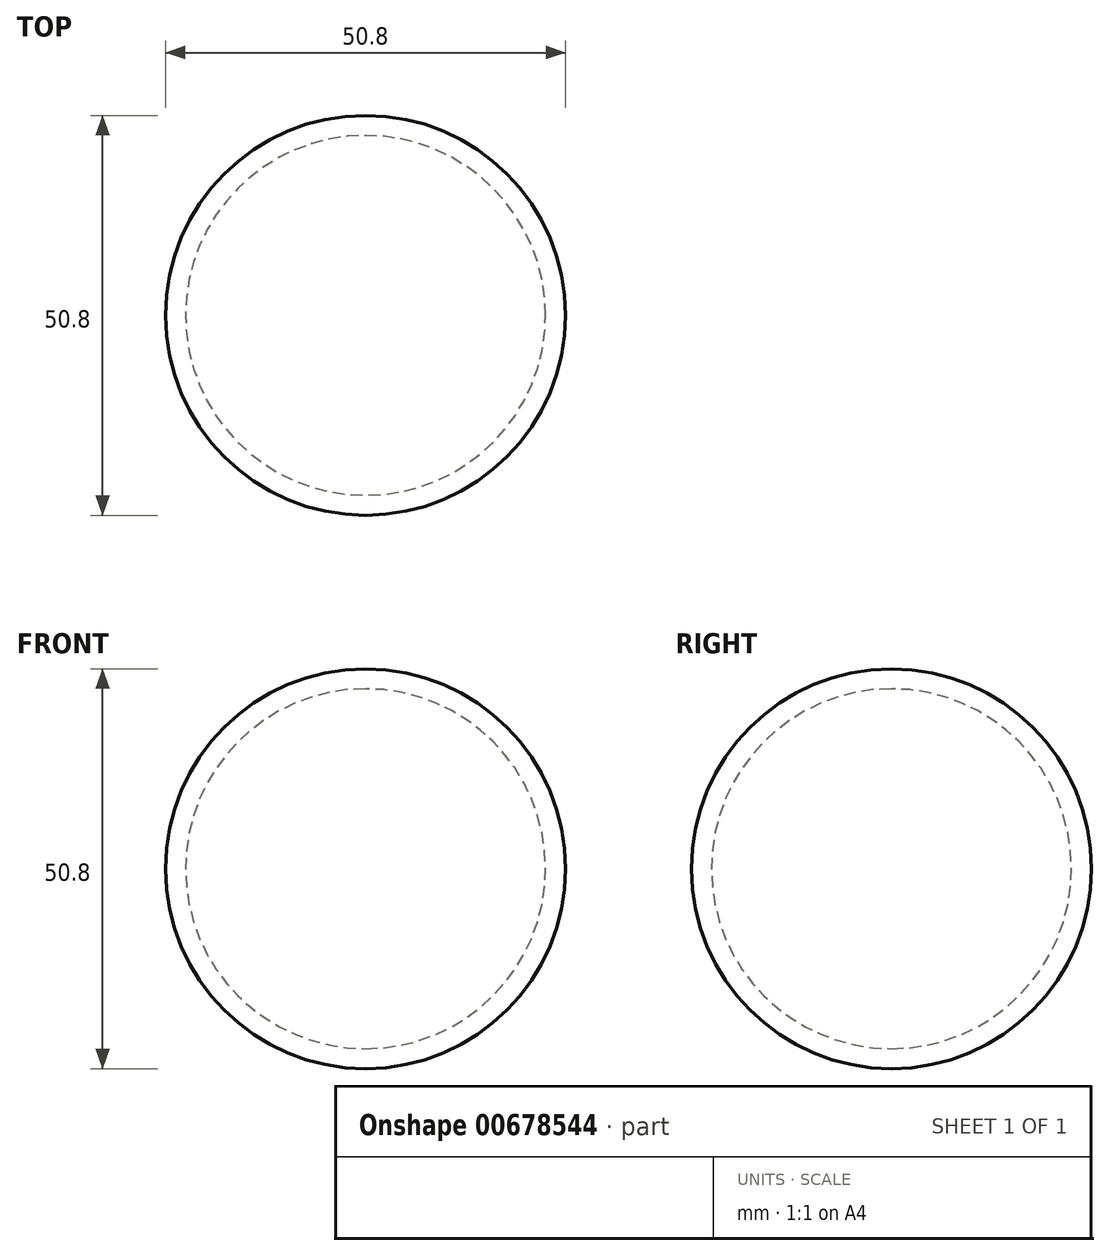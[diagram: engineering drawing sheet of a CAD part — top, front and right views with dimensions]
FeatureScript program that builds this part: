
annotation { "Feature Type Name" : "Feature", "Feature Type Description" : "" }
export const myFeature = defineFeature(function(context is Context, id is Id, definition is map)
    precondition{}
    {
        {
            var Q0;
            Q0=qCreatedBy(makeId("Front.planeOp"),FACE);
            var sketch = newSketch(context, id + "F0", { "sketchPlane" : qUnion([Q0])});
            skArc(sketch, "E0", {"start": v(0, -25.4) * mm, "mid": v(-25.4, 0) * mm, "end": v(0, 25.4) * mm});
            skLineSegment(sketch, "E1", {"start": v(0, 25.4) * mm, "end": v(0, 22.86) * mm});
            skLineSegment(sketch, "E2", {"start": v(0, -25.4) * mm, "end": v(0, -22.86) * mm});
            skArc(sketch, "E3", {"start": v(0, -22.86) * mm, "mid": v(-22.86, 0) * mm, "end": v(0, 22.86) * mm});
            skSolve(sketch);
        }
        {
            var Q0;
            Q0 = qSketchRegion(id + "F0", true);
            var Q1;
            Q1=sQuery(id+"F0.wireOp",EDGE,"E1");
            revolve(context, id + "F1", {"entities" : qUnion([Q0]), "axis" : qUnion([Q1]), "revolveType" : RevolveType.FULL});
        }
    });
